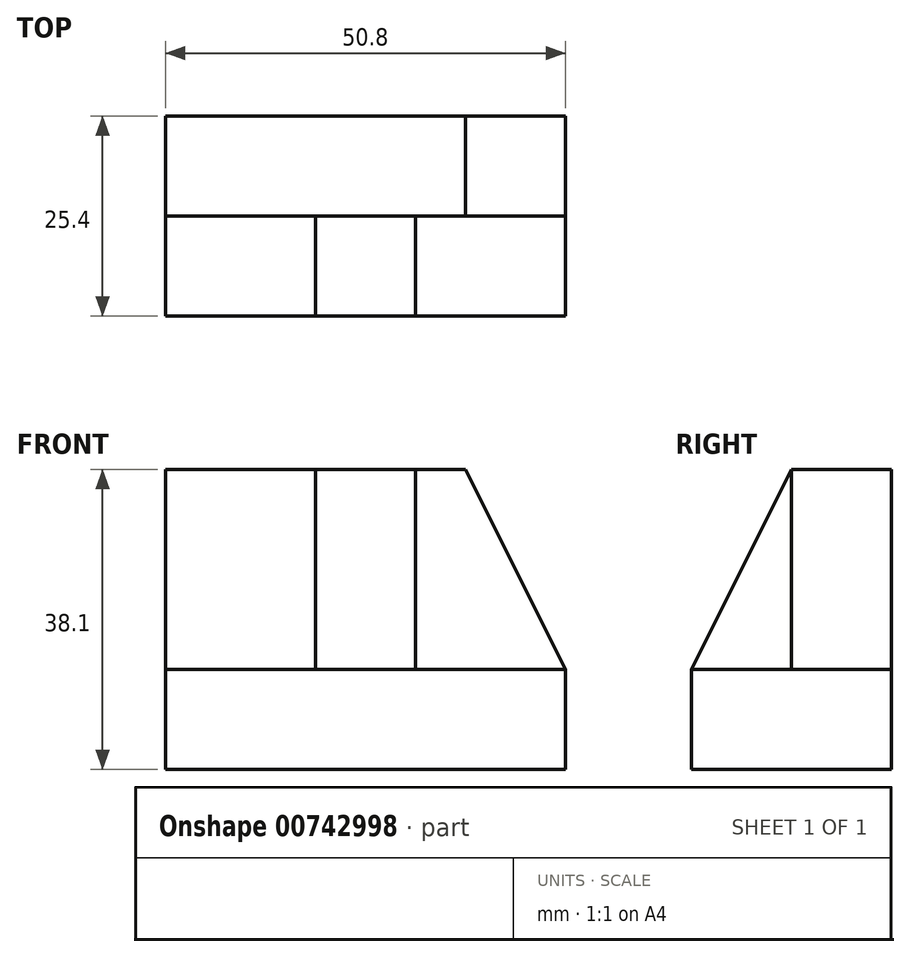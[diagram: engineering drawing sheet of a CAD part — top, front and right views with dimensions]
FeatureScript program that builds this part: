
annotation { "Feature Type Name" : "Feature", "Feature Type Description" : "" }
export const myFeature = defineFeature(function(context is Context, id is Id, definition is map)
    precondition{}
    {
        {
            var Q0;
            Q0=qCreatedBy(makeId("Front.planeOp"),FACE);
            var sketch = newSketch(context, id + "F0", { "sketchPlane" : qUnion([Q0])});
            skLineSegment(sketch, "E0", {"start": v(0, 0) * mm, "end": v(50.8, 0) * mm});
            skLineSegment(sketch, "E1", {"start": v(50.8, 0) * mm, "end": v(50.8, 38.1) * mm});
            skLineSegment(sketch, "E2", {"start": v(50.8, 38.1) * mm, "end": v(0, 38.1) * mm});
            skLineSegment(sketch, "E3", {"start": v(0, 38.1) * mm, "end": v(0, 0) * mm});
            skSolve(sketch);
        }
        {
            var Q0;
            Q0 = qSketchRegion(id + "F0", true);
            extrude(context, id + "F1", {"entities" : qUnion([Q0]), "depth" : 25.4 * mm, "offsetDistance" : 25.4 * mm});
        }
        {
            var Q0;
            Q0=makeQuery(id+"F1.opExtrude","SWEPT_FACE",FACE,{"disambiguationData":[OSD([sQuery(id+"F0.wireOp",EDGE,"E3")])]});
            var sketch = newSketch(context, id + "F2", { "sketchPlane" : qUnion([Q0])});
            skLineSegment(sketch, "E4", {"start": v(12.7, 38.1) * mm, "end": v(12.7, 19.05) * mm});
            skLineSegment(sketch, "E5", {"start": v(12.7, 19.05) * mm, "end": v(25.4, 19.05) * mm});
            skSolve(sketch);
        }
        {
            var Q0;
            {var subQ0=sQuery(id+"F2.wireOp",EDGE,"E4");Q0=makeQuery(id+"F2.imprint","IMPRINT",FACE,{"disambiguationData":[TD([[makeQuery(id+"F2.imprint","IMPRINT",EDGE,{"derivedFrom":subQ0}),1.0]])]});}
            extrude(context, id + "F3", {"entities" : qUnion([Q0]), "operationType" : NewBodyOperationType.REMOVE, "oppositeDirection" : true, "depth" : 19.05 * mm, "offsetDistance" : 25.4 * mm});
        }
        {
            var Q0;
            Q0=makeQuery(id+"F1.opExtrude","SWEPT_FACE",FACE,{"disambiguationData":[OSD([sQuery(id+"F0.wireOp",EDGE,"E1")])]});
            var sketch = newSketch(context, id + "F4", { "sketchPlane" : qUnion([Q0])});
            skLineSegment(sketch, "E6", {"start": v(-12.7, 38.1) * mm, "end": v(-12.7, 12.7) * mm});
            skLineSegment(sketch, "E7", {"start": v(-12.7, 12.7) * mm, "end": v(-25.4, 12.7) * mm});
            skSolve(sketch);
        }
        {
            var Q0;
            Q0 = qSketchRegion(id + "F4", true);
            var Q1;
            {var subQ0=sQuery(id+"F4.wireOp",EDGE,"E6");Q1=makeQuery(id+"F4.imprint","IMPRINT",FACE,{"disambiguationData":[TD([[makeQuery(id+"F4.imprint","IMPRINT",EDGE,{"derivedFrom":subQ0}),-1.0]])]});}
            extrude(context, id + "F5", {"entities" : qUnion([Q0, Q1]), "operationType" : NewBodyOperationType.REMOVE, "oppositeDirection" : true, "depth" : 19.05 * mm, "offsetDistance" : 25.4 * mm});
        }
        {
            var Q0;
            Q0=makeQuery(id+"F1.opExtrude","SWEPT_FACE",FACE,{"disambiguationData":[OSD([sQuery(id+"F0.wireOp",EDGE,"E3")])]});
            var sketch = newSketch(context, id + "F6", { "sketchPlane" : qUnion([Q0])});
            skLineSegment(sketch, "E8", {"start": v(12.7, 38.1) * mm, "end": v(12.7, 12.7) * mm});
            skLineSegment(sketch, "E9", {"start": v(12.7, 12.7) * mm, "end": v(25.4, 12.7) * mm});
            skSolve(sketch);
        }
        {
            var Q0;
            Q0 = qSketchRegion(id + "F6", true);
            var Q1;
            {var subQ2=sQuery(id+"F6.wireOp",EDGE,"E9");Q1=makeQuery(id+"F6.imprint","IMPRINT",FACE,{"disambiguationData":[TD([[makeQuery(id+"F6.imprint","IMPRINT",EDGE,{"derivedFrom":subQ2}),1.0]])]});}
            extrude(context, id + "F7", {"entities" : qUnion([Q0, Q1]), "operationType" : NewBodyOperationType.REMOVE, "oppositeDirection" : true, "depth" : 19.05 * mm, "offsetDistance" : 25.4 * mm});
        }
        {
            var Q0;
            {var subQ0=sQuery(id+"F2.wireOp",EDGE,"E5");var subQ1=sQuery(id+"F0.wireOp",EDGE,"E3");Q0=makeQuery(id+"F7.boolean.opBoolean","MERGE",FACE,{"derivedFrom":[makeQuery(id+"F3.boolean.opBoolean","COPY",FACE,{"derivedFrom":makeQuery(id+"F3.opExtrude","CAP_FACE",FACE,{"disambiguationData":[OSD([sQuery(id+"F0.wireOp",EDGE,"E2"),subQ1,sQuery(id+"F2.wireOp",EDGE,"E4"),subQ0])],"isStart":false})}),makeQuery(id+"F7.opExtrude","CAP_FACE",FACE,{"disambiguationData":[OSD([subQ1,subQ0,sQuery(id+"F6.wireOp",EDGE,"E8"),sQuery(id+"F6.wireOp",EDGE,"E9")])],"isStart":false})]});}
            var sketch = newSketch(context, id + "F8", { "sketchPlane" : qUnion([Q0])});
            skLineSegment(sketch, "E10", {"start": v(12.7, 38.1) * mm, "end": v(25.4, 12.7) * mm});
            skSolve(sketch);
        }
        {
            var Q0;
            Q0 = qSketchRegion(id + "F8", true);
            var Q1;
            Q1=makeQuery(id+"F8.imprint","IMPRINT",FACE,{"disambiguationData":[TD([[makeQuery(id+"F8.imprint","IMPRINT",EDGE,{"derivedFrom":sQuery(id+"F8.wireOp",EDGE,"E10")}),1.0]])]});
            extrude(context, id + "F9", {"entities" : qUnion([Q0, Q1]), "operationType" : NewBodyOperationType.REMOVE, "oppositeDirection" : true, "depth" : 25.4 * mm, "offsetDistance" : 25.4 * mm});
        }
        {
            var Q0;
            Q0=makeQuery(id+"F1.opExtrude","CAP_FACE",FACE,{"disambiguationData":[OSD([sQuery(id+"F0.wireOp",EDGE,"E0"),sQuery(id+"F0.wireOp",EDGE,"E1"),sQuery(id+"F0.wireOp",EDGE,"E2"),sQuery(id+"F0.wireOp",EDGE,"E3")])],"isStart":true});
            var sketch = newSketch(context, id + "F10", { "sketchPlane" : qUnion([Q0])});
            skLineSegment(sketch, "E11", {"start": v(-38.1, 38.1) * mm, "end": v(-50.8, 12.7) * mm});
            skSolve(sketch);
        }
        {
            var Q0;
            Q0 = qSketchRegion(id + "F10", true);
            var Q1;
            {var subQ0=sQuery(id+"F10.wireOp",EDGE,"E11");Q1=makeQuery(id+"F10.imprint","IMPRINT",FACE,{"disambiguationData":[TD([[makeQuery(id+"F10.imprint","IMPRINT",EDGE,{"derivedFrom":subQ0}),-1.0]])]});}
            extrude(context, id + "F11", {"entities" : qUnion([Q0, Q1]), "operationType" : NewBodyOperationType.REMOVE, "oppositeDirection" : true, "depth" : 25.4 * mm, "offsetDistance" : 25.4 * mm});
        }
    });
